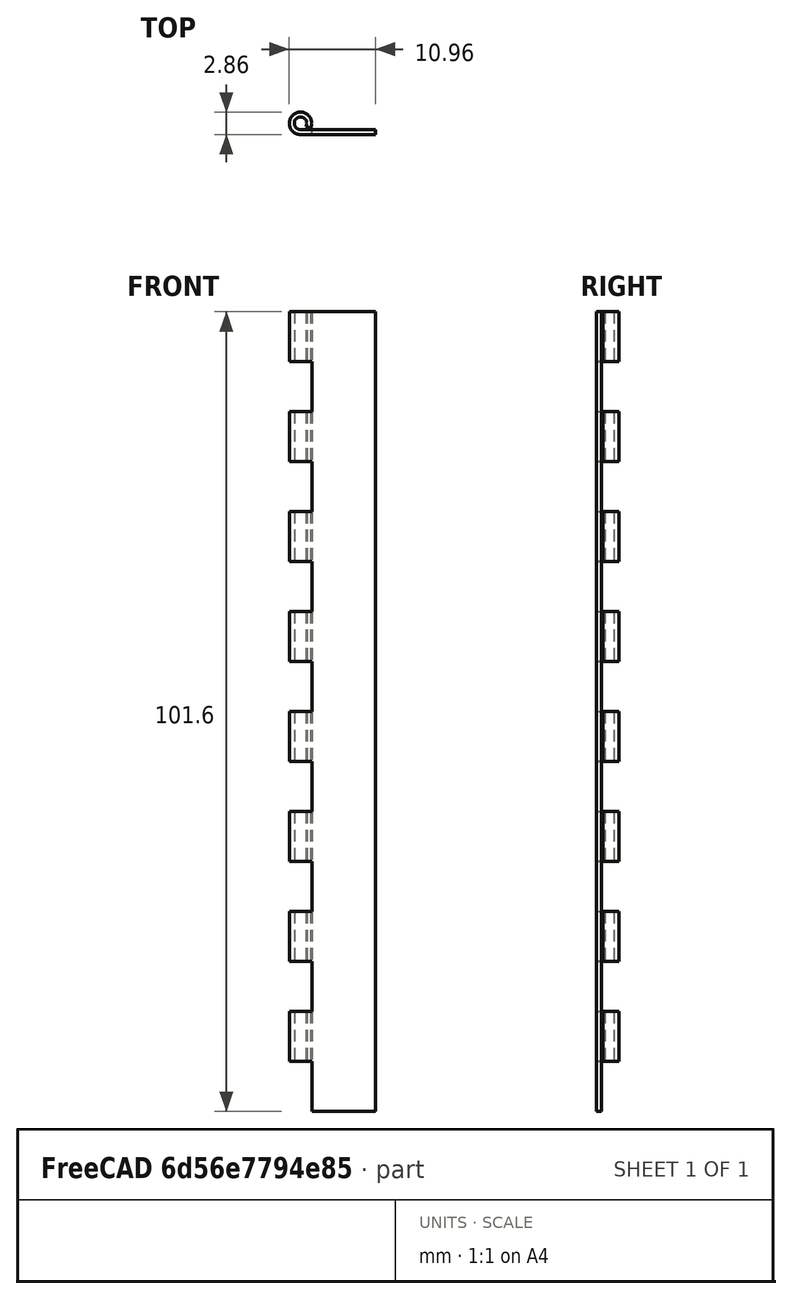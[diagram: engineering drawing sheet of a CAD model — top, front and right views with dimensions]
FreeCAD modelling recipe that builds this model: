
FCSTD DOCUMENT  (FreeCAD 0.19R24267 (Git))
Label: hinge_r-4
License: All rights reserved
LicenseURL: http://en.wikipedia.org/wiki/All_rights_reserved
objects: Part::Feature×1, Sketcher::SketchObject×1, Part::Extrusion×1, Part::Cut×1
note: 4 computed .brp shape members not serialized (recipe doc carries the construction recipe); baked Part::Feature solids carry a one-line shape summary decoded from their .brp

FEATURE [Part::Feature] Solid
  shape: bbox 10.95 x 2.858 x 304.8 mm, 244 faces (baked)
FEATURE [Sketcher::SketchObject] Sketch
  FullyConstrained = false
  MapMode = 5
  Placement = pos=(0,0,152.4) rot=(0,0,1;0rad)
  Support = -> [Solid]
  sketch-geometry (4):
    g0: LineSegment StartX=-3.61622 StartY=2.20045 StartZ=0 EndX=12.2431 EndY=2.20045 EndZ=0
    g1: LineSegment StartX=12.2431 StartY=2.20045 StartZ=0 EndX=12.2431 EndY=-2.92226 EndZ=0
    g2: LineSegment StartX=12.2431 StartY=-2.92226 StartZ=0 EndX=-3.61622 EndY=-2.92226 EndZ=0
    g3: LineSegment StartX=-3.61622 StartY=-2.92226 StartZ=0 EndX=-3.61622 EndY=2.20045 EndZ=0
  constraints (8):
    c: Coincident(g0,g1)
    c: Coincident(g1,g2)
    c: Coincident(g2,g3)
    c: Coincident(g3,g0)
    c: Horizontal(g0)
    c: Horizontal(g2)
    c: Vertical(g1)
    c: Vertical(g3)
FEATURE [Part::Extrusion] Extrude
  Base = -> Sketch
  Dir = (0,0,1)
  DirMode = 2
  FaceMakerClass = Part::FaceMakerBullseye
  LengthFwd = 0
  LengthRev = 203.2
  Solid = true
  Symmetric = false
FEATURE [Part::Cut] Cut
  Base = -> Solid
  Tool = -> Extrude
